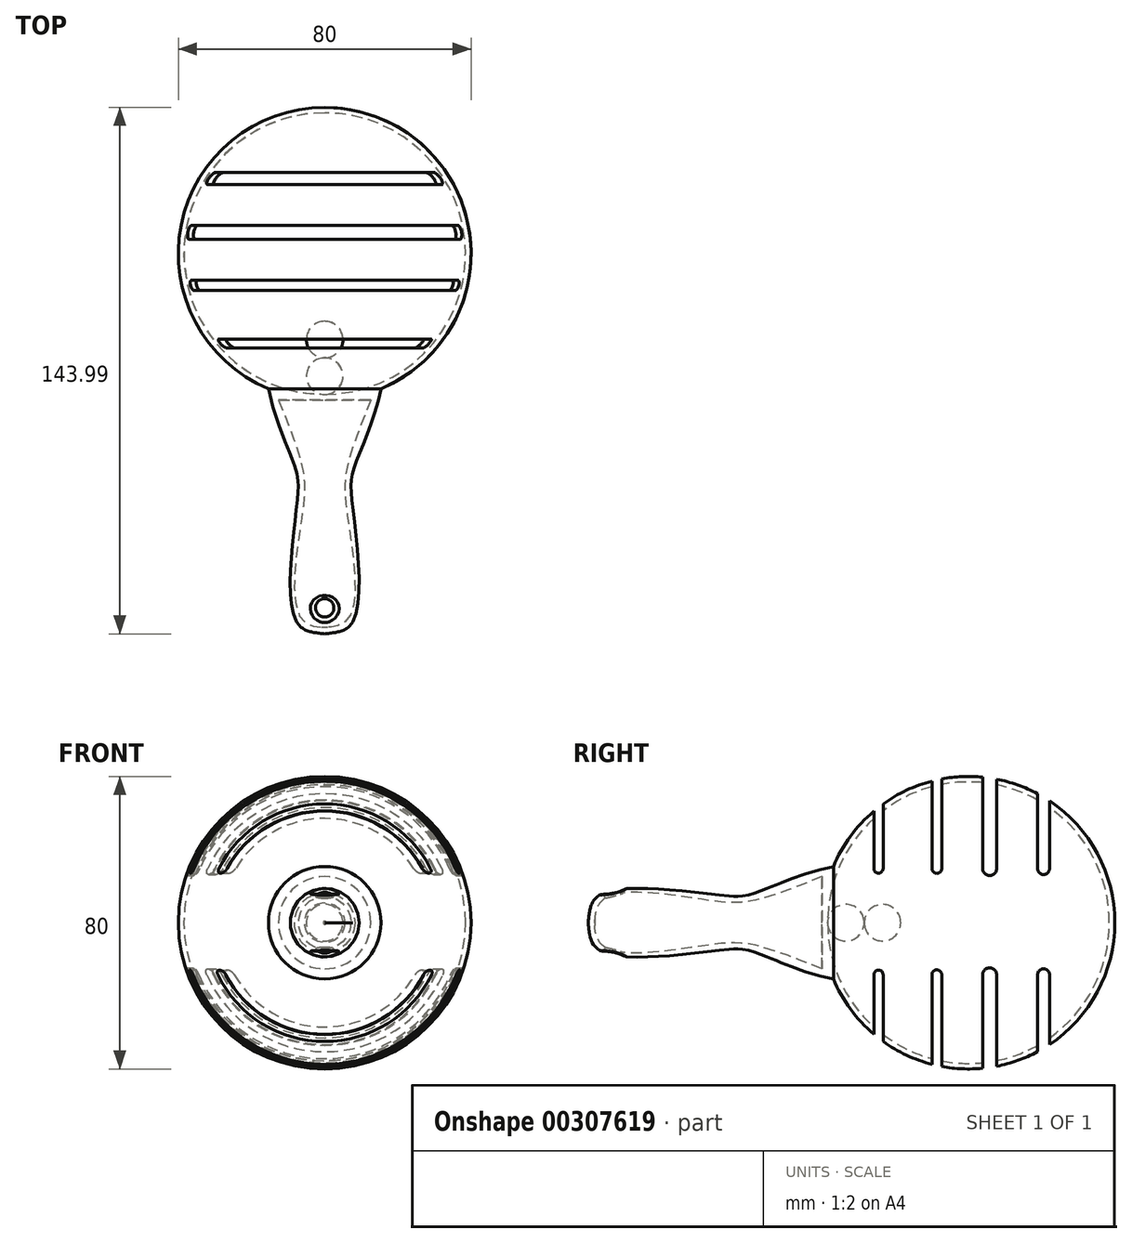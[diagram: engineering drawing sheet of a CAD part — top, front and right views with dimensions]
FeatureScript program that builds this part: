
annotation { "Feature Type Name" : "Feature", "Feature Type Description" : "" }
export const myFeature = defineFeature(function(context is Context, id is Id, definition is map)
    precondition{}
    {
        {
            var Q0;
            Q0=qCreatedBy(makeId("Top.planeOp"),FACE);
            var sketch = newSketch(context, id + "F0", { "sketchPlane" : qUnion([Q0])});
            skArc(sketch, "E0", {"start": v(15.37, 11) * mm, "mid": v(39.22, 55.77) * mm, "end": v(0, 87.93) * mm});
            skArc(sketch, "E1", {"start": v(0, 9.43) * mm, "mid": v(38.5, 47.93) * mm, "end": v(0, 86.43) * mm});
            skLineSegment(sketch, "E2", {"start": v(0, 87.93) * mm, "end": v(0, 86.43) * mm});
            skLineSegment(sketch, "E3.trimOffspring", {"start": v(0, 9.43) * mm, "end": v(0, 7.93) * mm});
            skLineSegment(sketch, "E4", {"start": v(0, -54.17) * mm, "end": v(0, -56.06) * mm, "construction": true});
            skLineSegment(sketch, "E5", {"start": v(0, -56.06) * mm, "end": v(15.37, -56.06) * mm, "construction": true});
            skLineSegment(sketch, "E6", {"start": v(15.37, -56.06) * mm, "end": v(15.37, 11) * mm, "construction": true});
            skFitSpline(sketch, "E7", {"points": [v(15.37, 11) * mm, v(7.94, -10.97) * mm, v(7.6, -20.62) * mm, v(7.69, -52.77) * mm, v(0, -56.06) * mm], "startDerivative": vector(-19.07, -97.58) * mm, "endDerivative": vector(-45.7, -6.65) * mm});
            skLineSegment(sketch, "E8", {"start": v(0, -56.06) * mm, "end": v(0, -54.17) * mm});
            skPoint(sketch, "E9", {"position": v(7.69, -56.06) * mm});
            skLineSegment(sketch, "E10", {"start": v(0, 7.93) * mm, "end": v(12.62, 7.93) * mm});
            skFitSpline(sketch, "E11", {"points": [v(12.62, 7.93) * mm, v(6.09, -10.8) * mm, v(6.2, -23.76) * mm, v(6.65, -51.52) * mm, v(0.85, -54.24) * mm, v(0, -54.17) * mm], "startDerivative": vector(-30.73, -76.87) * mm, "endDerivative": vector(-11.2, 1.96) * mm});
            skLineSegment(sketch, "E12.trimOffspring", {"start": v(0, 7.93) * mm, "end": v(0, 9.43) * mm});
            skFitSpline(sketch, "E13", {"points": [v(7.69, -52.77) * mm, v(6.96, -54.8) * mm, v(7.69, -56.06) * mm], "startDerivative": vector(-2.11, -3.97) * mm, "endDerivative": vector(2.26, -2.58) * mm});
            skLineSegment(sketch, "E14", {"start": v(0, -56.06) * mm, "end": v(7.69, -56.06) * mm});
            skSolve(sketch);
        }
        {
            var Q0;
            Q0=makeQuery(id+"F0.imprint","IMPRINT",FACE,{"disambiguationData":[TD([[makeQuery(id+"F0.imprint","IMPRINT",EDGE,{"derivedFrom":sQuery(id+"F0.wireOp",EDGE,"E0")}),1.0]])]});
            var Q1;
            Q1=sQuery(id+"F0.wireOp",EDGE,"E8");
            revolve(context, id + "F1", {"entities" : qUnion([Q0]), "axis" : qUnion([Q1]), "revolveType" : RevolveType.FULL});
        }
        {
            var Q0;
            Q0=qCreatedBy(makeId("Right.planeOp"),FACE);
            var sketch = newSketch(context, id + "F2", { "sketchPlane" : qUnion([Q0])});
            skLineSegment(sketch, "E15.bottom", {"start": v(22.06, 49.16) * mm, "end": v(24.6, 49.16) * mm});
            skLineSegment(sketch, "E15.top", {"start": v(22.06, -57.07) * mm, "end": v(24.6, -57.07) * mm});
            skLineSegment(sketch, "E15.left", {"start": v(22.06, 49.16) * mm, "end": v(22.06, 14.81) * mm});
            skLineSegment(sketch, "E15.right", {"start": v(24.6, 49.16) * mm, "end": v(24.6, 14.81) * mm});
            skLineSegment(sketch, "E16.bottom", {"start": v(37.93, 50.86) * mm, "end": v(40.6, 50.86) * mm});
            skLineSegment(sketch, "E16.top", {"start": v(37.93, -57.92) * mm, "end": v(40.6, -57.92) * mm});
            skLineSegment(sketch, "E16.left", {"start": v(37.93, 50.86) * mm, "end": v(37.93, 14.81) * mm});
            skLineSegment(sketch, "E16.right", {"start": v(40.6, 50.86) * mm, "end": v(40.6, 14.81) * mm});
            skLineSegment(sketch, "E17.bottom", {"start": v(51.8, 51.7) * mm, "end": v(55.62, 51.7) * mm});
            skLineSegment(sketch, "E17.top", {"start": v(51.8, -55.37) * mm, "end": v(55.62, -55.37) * mm});
            skLineSegment(sketch, "E17.left", {"start": v(51.8, 51.7) * mm, "end": v(51.8, 14.81) * mm});
            skLineSegment(sketch, "E17.right", {"start": v(55.62, 51.7) * mm, "end": v(55.62, 14.81) * mm});
            skLineSegment(sketch, "E18.bottom", {"start": v(66.82, 52) * mm, "end": v(70.07, 52) * mm});
            skLineSegment(sketch, "E18.top", {"start": v(66.82, -61.6) * mm, "end": v(70.07, -61.6) * mm});
            skLineSegment(sketch, "E18.left", {"start": v(66.82, 52) * mm, "end": v(66.82, 14.81) * mm});
            skLineSegment(sketch, "E18.right", {"start": v(70.07, 52) * mm, "end": v(70.07, 14.81) * mm});
            skLineSegment(sketch, "E19.trimOffspring", {"start": v(70.07, -14.23) * mm, "end": v(70.07, -61.6) * mm});
            skLineSegment(sketch, "E20.trimOffspring", {"start": v(66.82, -14.23) * mm, "end": v(66.82, -61.6) * mm});
            skLineSegment(sketch, "E21.trimOffspring", {"start": v(55.62, -14.23) * mm, "end": v(55.62, -55.37) * mm});
            skLineSegment(sketch, "E22.trimOffspring", {"start": v(51.8, -14.23) * mm, "end": v(51.8, -55.37) * mm});
            skLineSegment(sketch, "E23.trimOffspring", {"start": v(40.6, -14.23) * mm, "end": v(40.6, -57.92) * mm});
            skLineSegment(sketch, "E24.trimOffspring", {"start": v(37.93, -14.23) * mm, "end": v(37.93, -57.92) * mm});
            skLineSegment(sketch, "E25.trimOffspring", {"start": v(24.6, -14.23) * mm, "end": v(24.6, -57.07) * mm});
            skLineSegment(sketch, "E26.trimOffspring", {"start": v(22.06, -14.23) * mm, "end": v(22.06, -57.07) * mm});
            skPoint(sketch, "E27.visualSharp", {"position": v(24.6, 14.81) * mm});
            skLineSegment(sketch, "E27.filletArc", {"start": v(24.6, 14.81) * mm, "end": v(24.6, 14.81) * mm});
            skPoint(sketch, "E28.visualSharp", {"position": v(22.06, 14.81) * mm});
            skLineSegment(sketch, "E28.filletArc", {"start": v(22.06, 14.81) * mm, "end": v(22.06, 14.81) * mm});
            skPoint(sketch, "E29.visualSharp", {"position": v(37.93, 14.81) * mm});
            skLineSegment(sketch, "E29.filletArc", {"start": v(37.93, 14.81) * mm, "end": v(37.93, 14.81) * mm});
            skPoint(sketch, "E30.visualSharp", {"position": v(40.6, 14.81) * mm});
            skLineSegment(sketch, "E30.filletArc", {"start": v(40.6, 14.81) * mm, "end": v(40.6, 14.81) * mm});
            skPoint(sketch, "E31.visualSharp", {"position": v(51.8, 14.81) * mm});
            skLineSegment(sketch, "E31.filletArc", {"start": v(51.8, 14.81) * mm, "end": v(51.8, 14.81) * mm});
            skPoint(sketch, "E32.visualSharp", {"position": v(55.62, 14.81) * mm});
            skLineSegment(sketch, "E32.filletArc", {"start": v(55.62, 14.81) * mm, "end": v(55.62, 14.81) * mm});
            skPoint(sketch, "E33.visualSharp", {"position": v(66.82, 14.81) * mm});
            skLineSegment(sketch, "E33.filletArc", {"start": v(66.82, 14.81) * mm, "end": v(66.82, 14.81) * mm});
            skPoint(sketch, "E34.visualSharp", {"position": v(70.07, 14.81) * mm});
            skLineSegment(sketch, "E34.filletArc", {"start": v(70.07, 14.81) * mm, "end": v(70.07, 14.81) * mm});
            skPoint(sketch, "E35.visualSharp", {"position": v(70.07, -14.23) * mm});
            skLineSegment(sketch, "E35.filletArc", {"start": v(70.07, -14.23) * mm, "end": v(70.07, -14.23) * mm});
            skPoint(sketch, "E36.visualSharp", {"position": v(66.82, -14.23) * mm});
            skLineSegment(sketch, "E36.filletArc", {"start": v(66.82, -14.23) * mm, "end": v(66.82, -14.23) * mm});
            skPoint(sketch, "E37.visualSharp", {"position": v(55.62, -14.23) * mm});
            skLineSegment(sketch, "E37.filletArc", {"start": v(55.62, -14.23) * mm, "end": v(55.62, -14.23) * mm});
            skPoint(sketch, "E38.visualSharp", {"position": v(51.8, -14.23) * mm});
            skLineSegment(sketch, "E38.filletArc", {"start": v(51.8, -14.23) * mm, "end": v(51.8, -14.23) * mm});
            skPoint(sketch, "E39.visualSharp", {"position": v(40.6, -14.23) * mm});
            skLineSegment(sketch, "E39.filletArc", {"start": v(40.6, -14.23) * mm, "end": v(40.6, -14.23) * mm});
            skArc(sketch, "E40", {"start": v(22.06, 14.81) * mm, "mid": v(23.33, 13.55) * mm, "end": v(24.6, 14.81) * mm});
            skArc(sketch, "E41", {"start": v(37.93, 14.81) * mm, "mid": v(39.27, 13.47) * mm, "end": v(40.6, 14.81) * mm});
            skArc(sketch, "E42", {"start": v(51.8, 14.81) * mm, "mid": v(53.71, 12.9) * mm, "end": v(55.62, 14.81) * mm});
            skArc(sketch, "E43", {"start": v(66.82, 14.81) * mm, "mid": v(68.44, 13.2) * mm, "end": v(70.07, 14.81) * mm});
            skArc(sketch, "E44", {"start": v(70.07, -14.23) * mm, "mid": v(68.44, -12.6) * mm, "end": v(66.82, -14.23) * mm});
            skArc(sketch, "E45", {"start": v(55.62, -14.23) * mm, "mid": v(53.71, -12.32) * mm, "end": v(51.8, -14.23) * mm});
            skArc(sketch, "E46", {"start": v(40.6, -14.23) * mm, "mid": v(39.27, -12.89) * mm, "end": v(37.93, -14.23) * mm});
            skArc(sketch, "E47", {"start": v(24.6, -14.23) * mm, "mid": v(23.33, -12.96) * mm, "end": v(22.06, -14.23) * mm});
            skSolve(sketch);
        }
        {
            var Q0;
            Q0=makeQuery(id+"F2.imprint","IMPRINT",FACE,{"disambiguationData":[TD([[makeQuery(id+"F2.imprint","IMPRINT",EDGE,{"derivedFrom":sQuery(id+"F2.wireOp",EDGE,"E18.bottom")}),-1.0]])]});
            var Q1;
            Q1=makeQuery(id+"F2.imprint","IMPRINT",FACE,{"disambiguationData":[TD([[makeQuery(id+"F2.imprint","IMPRINT",EDGE,{"derivedFrom":sQuery(id+"F2.wireOp",EDGE,"E17.bottom")}),-1.0]])]});
            var Q2;
            Q2=makeQuery(id+"F2.imprint","IMPRINT",FACE,{"disambiguationData":[TD([[makeQuery(id+"F2.imprint","IMPRINT",EDGE,{"derivedFrom":sQuery(id+"F2.wireOp",EDGE,"E16.bottom")}),-1.0]])]});
            var Q3;
            Q3=makeQuery(id+"F2.imprint","IMPRINT",FACE,{"disambiguationData":[TD([[makeQuery(id+"F2.imprint","IMPRINT",EDGE,{"derivedFrom":sQuery(id+"F2.wireOp",EDGE,"E15.bottom")}),-1.0]])]});
            var Q4;
            Q4=makeQuery(id+"F2.imprint","IMPRINT",FACE,{"disambiguationData":[TD([[makeQuery(id+"F2.imprint","IMPRINT",EDGE,{"derivedFrom":sQuery(id+"F2.wireOp",EDGE,"E15.top")}),1.0]])]});
            var Q5;
            Q5=makeQuery(id+"F2.imprint","IMPRINT",FACE,{"disambiguationData":[TD([[makeQuery(id+"F2.imprint","IMPRINT",EDGE,{"derivedFrom":sQuery(id+"F2.wireOp",EDGE,"E16.top")}),1.0]])]});
            var Q6;
            Q6=makeQuery(id+"F2.imprint","IMPRINT",FACE,{"disambiguationData":[TD([[makeQuery(id+"F2.imprint","IMPRINT",EDGE,{"derivedFrom":sQuery(id+"F2.wireOp",EDGE,"E17.top")}),1.0]])]});
            var Q7;
            Q7=makeQuery(id+"F2.imprint","IMPRINT",FACE,{"disambiguationData":[TD([[makeQuery(id+"F2.imprint","IMPRINT",EDGE,{"derivedFrom":sQuery(id+"F2.wireOp",EDGE,"E18.top")}),1.0]])]});
            extrude(context, id + "F3", {"entities" : qUnion([Q0, Q1, Q2, Q3, Q4, Q5, Q6, Q7]), "operationType" : NewBodyOperationType.REMOVE, "endBound" : BoundingType.SYMMETRIC, "oppositeDirection" : true, "depth" : 100 * mm});
        }
        {
            var Q0;
            Q0=qCreatedBy(makeId("Top.planeOp"),FACE);
            var sketch = newSketch(context, id + "F4", { "sketchPlane" : qUnion([Q0])});
            skLineSegment(sketch, "E48", {"start": v(0, 9.43) * mm, "end": v(0, 19.43) * mm, "construction": true});
            skLineSegment(sketch, "E49", {"start": v(0, 19.43) * mm, "end": v(0, 29.43) * mm, "construction": true});
            skArc(sketch, "E50", {"start": v(0, 9.43) * mm, "mid": v(5, 14.24) * mm, "end": v(0.38, 19.41) * mm});
            skLineSegment(sketch, "E51", {"start": v(0, 19.43) * mm, "end": v(0, 19.43) * mm});
            skLineSegment(sketch, "E52", {"start": v(0, 29.43) * mm, "end": v(0, 9.43) * mm});
            skLineSegment(sketch, "E53", {"start": v(0.03, 19.43) * mm, "end": v(0.03, 19.43) * mm});
            skLineSegment(sketch, "E54", {"start": v(0.38, 19.41) * mm, "end": v(0.38, 19.44) * mm});
            skArc(sketch, "E55.trimOffspring", {"start": v(0.38, 19.44) * mm, "mid": v(5, 24.62) * mm, "end": v(0, 29.43) * mm});
            skSolve(sketch);
        }
        {
            var Q0;
            {var subQ0=sQuery(id+"F4.wireOp",EDGE,"E50");Q0=makeQuery(id+"F4.imprint","IMPRINT",FACE,{"disambiguationData":[TD([[makeQuery(id+"F4.imprint","IMPRINT",EDGE,{"derivedFrom":subQ0}),1.0]])]});}
            var Q1;
            {var subQ0=sQuery(id+"F4.wireOp",EDGE,"E51");Q1=makeQuery(id+"F4.imprint","IMPRINT",FACE,{"disambiguationData":[TD([[makeQuery(id+"F4.imprint","IMPRINT",EDGE,{"derivedFrom":subQ0}),1.0]])]});}
            var Q2;
            Q2=sQuery(id+"F4.wireOp",EDGE,"E52");
            revolve(context, id + "F5", {"operationType" : NewBodyOperationType.ADD, "entities" : qUnion([Q0, Q1]), "axis" : qUnion([Q2]), "revolveType" : RevolveType.FULL});
        }
        {
            var Q0;
            Q0=qCreatedBy(makeId("Top.planeOp"),FACE);
            var sketch = newSketch(context, id + "F6", { "sketchPlane" : qUnion([Q0])});
            skCircle(sketch, "E56", {"center": v(0, -48.94) * mm, "radius": 2.5 * mm});
            skSolve(sketch);
        }
        {
            var Q0;
            Q0 = qSketchRegion(id + "F6", true);
            extrude(context, id + "F7", {"entities" : qUnion([Q0]), "operationType" : NewBodyOperationType.REMOVE, "endBound" : BoundingType.SYMMETRIC, "oppositeDirection" : true, "depth" : 90 * mm});
        }
        {
            var Q0;
            Q0=makeQuery(id+"F7.boolean.opBoolean","INTERSECT",EDGE,{"disambiguationData":[OD(1.0)],"derivedFrom":[makeQuery(id+"F1.opRevolve","SWEPT_FACE",FACE,{"disambiguationData":[OSD([sQuery(id+"F0.wireOp",EDGE,"E7")])]}),makeQuery(id+"F7.opExtrude","SWEPT_FACE",FACE,{"disambiguationData":[OSD([sQuery(id+"F6.wireOp",EDGE,"E56")])]})]});
            var Q1;
            Q1=makeQuery(id+"F7.boolean.opBoolean","INTERSECT",EDGE,{"disambiguationData":[OD(0.0)],"derivedFrom":[makeQuery(id+"F1.opRevolve","SWEPT_FACE",FACE,{"disambiguationData":[OSD([sQuery(id+"F0.wireOp",EDGE,"E7")])]}),makeQuery(id+"F7.opExtrude","SWEPT_FACE",FACE,{"disambiguationData":[OSD([sQuery(id+"F6.wireOp",EDGE,"E56")])]})]});
            fillet(context, id + "F8", {"entities" : qUnion([Q0, Q1]), "radius" : 1 * mm, "tangentPropagation" : true, "allowEdgeOverflow" : false});
        }
        {
            var Q0;
            Q0=qCreatedBy(makeId("Top.planeOp"),FACE);
            var sketch = newSketch(context, id + "F9", { "sketchPlane" : qUnion([Q0])});
            skArc(sketch, "E57", {"start": v(-60.41, 22.95) * mm, "mid": v(-52.15, 31.21) * mm, "end": v(-60.41, 39.48) * mm});
            skLineSegment(sketch, "E58", {"start": v(-60.41, 39.48) * mm, "end": v(-60.41, 22.95) * mm});
            skSolve(sketch);
        }
        {
            var Q0;
            Q0=makeQuery(id+"F9.imprint","IMPRINT",FACE,{"disambiguationData":[TD([[makeQuery(id+"F9.imprint","IMPRINT",EDGE,{"derivedFrom":sQuery(id+"F9.wireOp",EDGE,"E57")}),1.0]])]});
            var Q1;
            Q1=sQuery(id+"F9.wireOp",EDGE,"E58");
            revolve(context, id + "F10", {"entities" : qUnion([Q0]), "axis" : qUnion([Q1]), "revolveType" : RevolveType.FULL});
        }
        {
            var Q0;
            Q0=makeQuery(id+"F10.opRevolve","SWEPT_BODY",BODY,{"disambiguationData":[OSD([sQuery(id+"F9.wireOp",EDGE,"E57"),sQuery(id+"F9.wireOp",EDGE,"E58")])]});
            deleteBodies(context, id + "F11", {"entities" : qUnion([Q0])});
        }
        {
            var Q0;
            Q0=makeQuery(id+"F2.imprint","IMPRINT",FACE,{"disambiguationData":[TD([[makeQuery(id+"F2.imprint","IMPRINT",EDGE,{"derivedFrom":sQuery(id+"F2.wireOp",EDGE,"E15.bottom")}),-1.0]])]});
            var Q1;
            Q1=makeQuery(id+"F2.imprint","IMPRINT",FACE,{"disambiguationData":[TD([[makeQuery(id+"F2.imprint","IMPRINT",EDGE,{"derivedFrom":sQuery(id+"F2.wireOp",EDGE,"E16.bottom")}),-1.0]])]});
            var Q2;
            Q2=makeQuery(id+"F2.imprint","IMPRINT",FACE,{"disambiguationData":[TD([[makeQuery(id+"F2.imprint","IMPRINT",EDGE,{"derivedFrom":sQuery(id+"F2.wireOp",EDGE,"E17.bottom")}),-1.0]])]});
            var Q3;
            Q3=makeQuery(id+"F2.imprint","IMPRINT",FACE,{"disambiguationData":[TD([[makeQuery(id+"F2.imprint","IMPRINT",EDGE,{"derivedFrom":sQuery(id+"F2.wireOp",EDGE,"E18.bottom")}),-1.0]])]});
            var Q4;
            Q4=makeQuery(id+"F2.imprint","IMPRINT",FACE,{"disambiguationData":[TD([[makeQuery(id+"F2.imprint","IMPRINT",EDGE,{"derivedFrom":sQuery(id+"F2.wireOp",EDGE,"E18.top")}),1.0]])]});
            var Q5;
            Q5=makeQuery(id+"F2.imprint","IMPRINT",FACE,{"disambiguationData":[TD([[makeQuery(id+"F2.imprint","IMPRINT",EDGE,{"derivedFrom":sQuery(id+"F2.wireOp",EDGE,"E17.top")}),1.0]])]});
            var Q6;
            Q6=makeQuery(id+"F2.imprint","IMPRINT",FACE,{"disambiguationData":[TD([[makeQuery(id+"F2.imprint","IMPRINT",EDGE,{"derivedFrom":sQuery(id+"F2.wireOp",EDGE,"E16.top")}),1.0]])]});
            var Q7;
            Q7=makeQuery(id+"F2.imprint","IMPRINT",FACE,{"disambiguationData":[TD([[makeQuery(id+"F2.imprint","IMPRINT",EDGE,{"derivedFrom":sQuery(id+"F2.wireOp",EDGE,"E15.top")}),1.0]])]});
            extrude(context, id + "F12", {"entities" : qUnion([Q0, Q1, Q2, Q3, Q4, Q5, Q6, Q7]), "operationType" : NewBodyOperationType.REMOVE, "endBound" : BoundingType.SYMMETRIC, "oppositeDirection" : true, "depth" : 80 * mm});
        }
        {
            var Q0;
            Q0=makeQuery(id+"F2.imprint","IMPRINT",FACE,{"disambiguationData":[TD([[makeQuery(id+"F2.imprint","IMPRINT",EDGE,{"derivedFrom":sQuery(id+"F2.wireOp",EDGE,"E15.bottom")}),-1.0]])]});
            var Q1;
            Q1=makeQuery(id+"F2.imprint","IMPRINT",FACE,{"disambiguationData":[TD([[makeQuery(id+"F2.imprint","IMPRINT",EDGE,{"derivedFrom":sQuery(id+"F2.wireOp",EDGE,"E16.bottom")}),-1.0]])]});
            var Q2;
            Q2=makeQuery(id+"F2.imprint","IMPRINT",FACE,{"disambiguationData":[TD([[makeQuery(id+"F2.imprint","IMPRINT",EDGE,{"derivedFrom":sQuery(id+"F2.wireOp",EDGE,"E17.bottom")}),-1.0]])]});
            var Q3;
            Q3=makeQuery(id+"F2.imprint","IMPRINT",FACE,{"disambiguationData":[TD([[makeQuery(id+"F2.imprint","IMPRINT",EDGE,{"derivedFrom":sQuery(id+"F2.wireOp",EDGE,"E18.bottom")}),-1.0]])]});
            var Q4;
            Q4=makeQuery(id+"F2.imprint","IMPRINT",FACE,{"disambiguationData":[TD([[makeQuery(id+"F2.imprint","IMPRINT",EDGE,{"derivedFrom":sQuery(id+"F2.wireOp",EDGE,"E18.top")}),1.0]])]});
            var Q5;
            Q5=makeQuery(id+"F2.imprint","IMPRINT",FACE,{"disambiguationData":[TD([[makeQuery(id+"F2.imprint","IMPRINT",EDGE,{"derivedFrom":sQuery(id+"F2.wireOp",EDGE,"E17.top")}),1.0]])]});
            var Q6;
            Q6=makeQuery(id+"F2.imprint","IMPRINT",FACE,{"disambiguationData":[TD([[makeQuery(id+"F2.imprint","IMPRINT",EDGE,{"derivedFrom":sQuery(id+"F2.wireOp",EDGE,"E16.top")}),1.0]])]});
            var Q7;
            Q7=makeQuery(id+"F2.imprint","IMPRINT",FACE,{"disambiguationData":[TD([[makeQuery(id+"F2.imprint","IMPRINT",EDGE,{"derivedFrom":sQuery(id+"F2.wireOp",EDGE,"E15.top")}),1.0]])]});
            extrude(context, id + "F13", {"entities" : qUnion([Q0, Q1, Q2, Q3, Q4, Q5, Q6, Q7]), "operationType" : NewBodyOperationType.REMOVE, "endBound" : BoundingType.SYMMETRIC, "oppositeDirection" : true, "depth" : 90 * mm});
        }
    });
